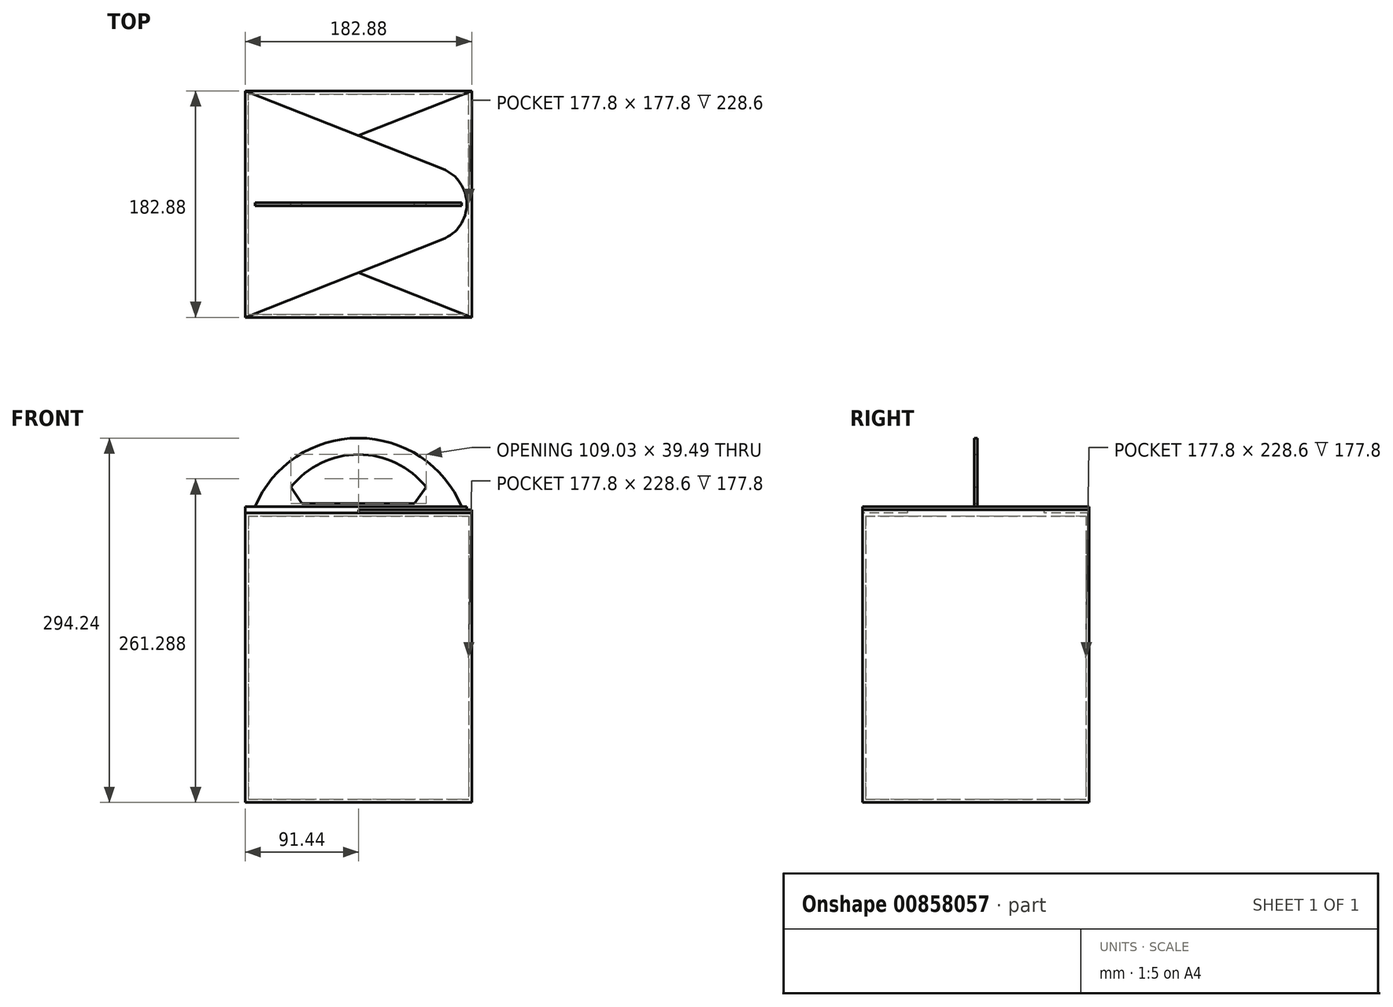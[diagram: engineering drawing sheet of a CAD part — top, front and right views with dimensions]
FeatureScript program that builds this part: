
annotation { "Feature Type Name" : "Feature", "Feature Type Description" : "" }
export const myFeature = defineFeature(function(context is Context, id is Id, definition is map)
    precondition{}
    {
        {
            var Q0;
            Q0=qCreatedBy(makeId("Top.planeOp"),FACE);
            var sketch = newSketch(context, id + "F0", { "sketchPlane" : qUnion([Q0])});
            skLineSegment(sketch, "E0.bottom", {"start": v(-91.44, -91.44) * mm, "end": v(91.44, -91.44) * mm});
            skLineSegment(sketch, "E0.top", {"start": v(-91.44, 91.44) * mm, "end": v(91.44, 91.44) * mm});
            skLineSegment(sketch, "E0.left", {"start": v(-91.44, -91.44) * mm, "end": v(-91.44, 91.44) * mm});
            skLineSegment(sketch, "E0.right", {"start": v(91.44, -91.44) * mm, "end": v(91.44, 91.44) * mm});
            skPoint(sketch, "E0.middle", {"position": v(0, 0) * mm});
            skSolve(sketch);
        }
        {
            var Q0;
            Q0=makeQuery(id+"F0.imprint","IMPRINT",FACE,{"disambiguationData":[TD([[makeQuery(id+"F0.imprint","IMPRINT",EDGE,{"derivedFrom":sQuery(id+"F0.wireOp",EDGE,"E0.bottom")}),1.0]])]});
            extrude(context, id + "F1", {"entities" : qUnion([Q0]), "depth" : 231.14 * mm, "offsetDistance" : 25.4 * mm});
        }
        {
            var Q0;
            Q0=makeQuery(id+"F1.opExtrude","CAP_FACE",FACE,{"disambiguationData":[OSD([sQuery(id+"F0.wireOp",EDGE,"E0.bottom"),sQuery(id+"F0.wireOp",EDGE,"E0.top"),sQuery(id+"F0.wireOp",EDGE,"E0.left"),sQuery(id+"F0.wireOp",EDGE,"E0.right")])],"isStart":false});
            shell(context, id + "F2", {"entities" : qUnion([Q0]), "thickness" : 2.54 * mm});
        }
        {
            var Q0;
            Q0=makeQuery(id+"F1.opExtrude","CAP_FACE",FACE,{"disambiguationData":[OSD([sQuery(id+"F0.wireOp",EDGE,"E0.bottom"),sQuery(id+"F0.wireOp",EDGE,"E0.top"),sQuery(id+"F0.wireOp",EDGE,"E0.left"),sQuery(id+"F0.wireOp",EDGE,"E0.right")])],"isStart":false});
            var sketch = newSketch(context, id + "F3", { "sketchPlane" : qUnion([Q0])});
            skLineSegment(sketch, "E1.bottom", {"start": v(-91.44, 91.44) * mm, "end": v(91.44, 91.44) * mm});
            skLineSegment(sketch, "E1.top", {"start": v(-91.44, -91.44) * mm, "end": v(91.44, -91.44) * mm});
            skLineSegment(sketch, "E1.left", {"start": v(-91.44, 91.44) * mm, "end": v(-91.44, -91.44) * mm});
            skLineSegment(sketch, "E1.right", {"start": v(91.44, 91.44) * mm, "end": v(91.44, -91.44) * mm});
            skPoint(sketch, "E1.middle", {"position": v(0, 0) * mm});
            skSolve(sketch);
        }
        {
            var Q0;
            Q0 = qSketchRegion(id + "F3", true);
            extrude(context, id + "F4", {"entities" : qUnion([Q0]), "operationType" : NewBodyOperationType.ADD, "depth" : 2.54 * mm, "offsetDistance" : 25.4 * mm});
        }
        {
            var Q0;
            Q0=makeQuery(id+"F4.opExtrude","CAP_FACE",FACE,{"disambiguationData":[OSD([sQuery(id+"F3.wireOp",EDGE,"E1.bottom"),sQuery(id+"F3.wireOp",EDGE,"E1.top"),sQuery(id+"F3.wireOp",EDGE,"E1.left"),sQuery(id+"F3.wireOp",EDGE,"E1.right")])],"isStart":false});
            var sketch = newSketch(context, id + "F5", { "sketchPlane" : qUnion([Q0])});
            skLineSegment(sketch, "E2", {"start": v(91.44, 91.44) * mm, "end": v(-68.06, 28.34) * mm});
            skLineSegment(sketch, "E3", {"start": v(-68.06, -28.34) * mm, "end": v(91.44, -91.44) * mm});
            skPoint(sketch, "E4.visualSharp", {"position": v(-139.7, 0) * mm});
            skArc(sketch, "E4.filletArc", {"start": v(-68.06, 28.34) * mm, "mid": v(-87.32, 0) * mm, "end": v(-68.06, -28.34) * mm});
            skSolve(sketch);
        }
        {
            var Q0;
            Q0=makeQuery(id+"F5.imprint","IMPRINT",FACE,{"disambiguationData":[TD([[makeQuery(id+"F5.imprint","IMPRINT",EDGE,{"derivedFrom":sQuery(id+"F5.wireOp",EDGE,"E2")}),1.0]])]});
            extrude(context, id + "F6", {"entities" : qUnion([Q0]), "operationType" : NewBodyOperationType.ADD, "depth" : 2.54 * mm, "offsetDistance" : 25.4 * mm});
        }
        {
            var Q0;
            Q0=makeQuery(id+"F4.opExtrude","CAP_FACE",FACE,{"disambiguationData":[OSD([sQuery(id+"F3.wireOp",EDGE,"E1.bottom"),sQuery(id+"F3.wireOp",EDGE,"E1.top"),sQuery(id+"F3.wireOp",EDGE,"E1.left"),sQuery(id+"F3.wireOp",EDGE,"E1.right")])],"isStart":false});
            var sketch = newSketch(context, id + "F7", { "sketchPlane" : qUnion([Q0])});
            skLineSegment(sketch, "E5", {"start": v(-91.44, 91.44) * mm, "end": v(68.06, 28.34) * mm});
            skLineSegment(sketch, "E6", {"start": v(68.06, -28.34) * mm, "end": v(-91.44, -91.44) * mm});
            skPoint(sketch, "E7.visualSharp", {"position": v(139.7, 0) * mm});
            skArc(sketch, "E7.filletArc", {"start": v(68.06, -28.34) * mm, "mid": v(87.32, 0) * mm, "end": v(68.06, 28.34) * mm});
            skLineSegment(sketch, "E8", {"start": v(-91.44, 91.44) * mm, "end": v(-91.44, -91.44) * mm});
            skSolve(sketch);
        }
        {
            var Q0;
            Q0 = qSketchRegion(id + "F7", true);
            extrude(context, id + "F8", {"entities" : qUnion([Q0]), "operationType" : NewBodyOperationType.ADD, "depth" : 5.08 * mm, "offsetDistance" : 25.4 * mm});
        }
        {
            var Q0;
            Q0=qCreatedBy(makeId("Front.planeOp"),FACE);
            var sketch = newSketch(context, id + "F9", { "sketchPlane" : qUnion([Q0])});
            skArc(sketch, "E9", {"start": v(83.24, 238.76) * mm, "mid": v(-0.16, 294.24) * mm, "end": v(-83.56, 238.76) * mm});
            skArc(sketch, "E10", {"start": v(54.51, 254.65) * mm, "mid": v(0, 281.03) * mm, "end": v(-54.51, 254.65) * mm});
            skLineSegment(sketch, "E11", {"start": v(-54.51, 254.65) * mm, "end": v(-45.64, 241.54) * mm});
            skLineSegment(sketch, "E12", {"start": v(-45.64, 241.54) * mm, "end": v(45.17, 241.54) * mm});
            skLineSegment(sketch, "E13", {"start": v(45.17, 241.54) * mm, "end": v(54.51, 254.65) * mm});
            skLineSegment(sketch, "E14", {"start": v(83.24, 238.76) * mm, "end": v(83.24, 236.87) * mm});
            skLineSegment(sketch, "E15", {"start": v(83.24, 236.87) * mm, "end": v(-83.63, 236.87) * mm});
            skLineSegment(sketch, "E16", {"start": v(-83.63, 236.87) * mm, "end": v(-83.56, 238.76) * mm});
            skSolve(sketch);
        }
        {
            var Q0;
            Q0 = qSketchRegion(id + "F9", true);
            var Q1;
            Q1 = qConstructionFilter(qBodyType(qCreatedBy(id + "F9" ,EDGE), BodyType.WIRE), ConstructionObject.NO);
            extrude(context, id + "F10", {"entities" : qUnion([Q0]), "operationType" : NewBodyOperationType.ADD, "surfaceEntities" : qUnion([Q1]), "endBound" : BoundingType.SYMMETRIC, "depth" : 2.54 * mm, "offsetDistance" : 25.4 * mm});
        }
    });
